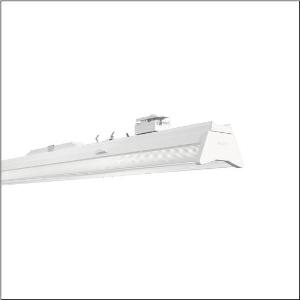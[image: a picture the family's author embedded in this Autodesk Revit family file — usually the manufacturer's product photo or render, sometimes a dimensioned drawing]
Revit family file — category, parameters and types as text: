
# Revit family: licross_r__21_performance_ho_52tm16dn4e5m_a06b
name_source: partatom
category: Lighting Fixtures
units: mm (PartAtom-declared; Revit-internal decimal feet)

## family parameters
Cut with Voids When Loaded = No
Host = Face
Light Source = No
Part Type = Normal
Room Calculation Point = No
Round Connector Dimension = Use Diameter
Shared = No

## types (1)
- --- (1 x LED, 14870 lm, 84.9 W, 4000K)
    Apparent Load = 85 VA
    CIE Flux Codes = 63 87 95 78 100
    Color Rendering = 80
    Color Temperature = 4000K
    Default Elevation = 1800 mm
    Description = Licross® 21 Performance HO, luminaire insert, of sheet steel, galvanised, coil coated, white, length: 1.500mm, width: 120mm, height: 123mm, LED rated luminous flux: 14.870lm, light colour: 840, control gear: DALI 2, with plug, 5-pole, with phase selection, mains connection: 220..240V, AC, 50/60Hz, rated input power: 85W, halogen-free wiring, primary light control with lens, of plastic, primary optical cover: cover, of PMMA, light emission: direct/indirect distribution, primary light characteristic: symmetric, protection rating (complete): IP40, insulation class (complete): insulation class I (protective earthing), certification: CE, ENEC, UKCA, protection symbol: D if used in an environment without relevant dust loads with corresponding accessories, impact resistance: IK06, permissible ambient temperature for indoor applications: -25..+35°C, corresponds to IFS (International Featured Standards) requirements for safety and quality in the food industry, reducing of maximum allowable ambient temperature of 5°C with ceiling mounting, LABS conformity tested according to VDMA 24364:2018-05, packaging unit: 1 piece
    Height = 114 mm
    Lamp = 1 x LED
    Lamp Light Flux = 14870 lm
    Lamp Power = 84.9 W
    Lamp count = 1
    Length = 1500 mm
    Luminous efficacy = 175 lm/W
    Manufacturer = Siteco
    ModVariant = No
    Model = 52TM16DN4E5M
    Mounting Place = Ceiling
    Mounting Type = Pendant
    Number of Poles = 1
    OnlyDefault = Yes
    Power Factor = 1
    Product Name = Licross® 21 Performance HO
    Product group = luminaire insert
    ProductGroupID = 901
    Protection Class = Protection class I
    Protection Degree = IP 40
    RLX_Detail_Level = 1
    RLX_Emergency_Light_Flux = 0 lm
    RLX_Emergency_Type = 0
    RLX_Emergency_Type_DB = No
    RlxData = <blob elided: 34085 chars, md5=44b86d54>
    Socket = socket
    Standby Power = 0 W
    System Light Flux = 14870 lm
    System Power = 85 W
    Type Comments = factory setting: luminous flux: 100 % | dim-lin: 254 | 484 mA
    Type Image = l_1256138.jpg
    URL = http://relux.com
    VarID = @adj_060959
    Voltage = 0 V
    Weight = 0.00 kg
    Width = 120 mm

## geometry (parser evidence)
native form markers: Blend x4, Sweep x11
no freeform markers — native parametric forms only
